# Revit family: Shower-Bath_and_Shower_Trim-KOHLER-Triton-K-TS6910_1
name_source: partatom
category: Plumbing Fixtures
revit_build: Autodesk Revit 2015 (Build: 20140606_1530(x64)
units: mm (PartAtom-declared; Revit-internal decimal feet)

## types (4) — shared parameters
ADA Compliant = No
Assembly Code = D2010700
CW Connection = No
Cold Water Inlet = Cold Water Inlet
Date Modified = 03/06/2019
Default Elevation = 42"
Drain Included = No
Finish = Kohler-Metal-CP-Polished_Chrome
HW Connection = Yes
Height = 6 7/16"
Hot Water Inlet = Tempered Water Inlet
Length = 7 1/8"
Manufacturer = KOHLER Co.
MasterFormat 1995 = 15410
MasterFormat 2004 = 22.41.23
Material = Premium Metal Construction
Panel Thickness = 0"
Pressure = 80.00 psi
Product Documentation Link = https://www.us.kohler.com
Product Name = Triton
Product Page URL = http://www.us.kohler.com
URL = https://www.us.kohler.com
Vent Connection = No
Waste Connection = No
Waste Water Outlet = Waste Water Outlet
WaterSense Certified = No
Width = 6 7/16"

## per-type parameters (varying)
| type | Cross_Handle | Description | Distance | Distance 1 | Distance 2 | Flow Rate | Handle_Clearance | Lever_Handle | Model | Shower_Head 1 | Shower_Head 2 | Type |
| 2.5 GPM, Cross Handle, CP-Polished Chrome | Yes | Rite-Temp shower valve trim with standard handle and 2.5 gpm showerhead | 2 5/8" | 5 5/8" | 1 3/8" | 3 GPM | 2 3/4" | No | K-TS6910-2A-CP | Yes | No | 1 |
| 2.5 GPM, Lever Handle, CP-Polished Chrome | No | Rite-Temp shower valve trim with lever handle and 2.5 gpm showerhead | 3 1/16" | 5 5/8" | 0" | 3 GPM | 2 7/16" | Yes | K-TS6910-4A-CP | Yes | No | 2 |
| 1.75 GPM, Cross Handle, CP-Polished Chrome | Yes | Rite-Temp shower valve trim with standard handle and 1.75 gpm showerhead | 2 5/8" | 4 5/16" | 1 3/8" | 2 GPM | 2 3/4" | No | K-TS6910-2G-CP | No | Yes | 3 |
| 1.75 GPM, Lever Handle, CP-Polished Chrome | No | Rite-Temp shower valve trim with lever handle and 1.75 gpm showerhead | 3 1/16" | 4 5/16" | 0" | 2 GPM | 2 7/16" | Yes | K-TS6910-4G-CP | No | Yes | 4 |

## geometry (parser evidence)
native form markers: Sweep x8
no freeform markers — native parametric forms only
